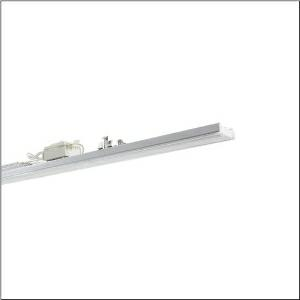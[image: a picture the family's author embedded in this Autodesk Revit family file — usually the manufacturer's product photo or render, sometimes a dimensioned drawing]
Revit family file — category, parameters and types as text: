
# Revit family: licross_11_recessed_ho_51tl18cn4c5m
name_source: partatom
category: Lighting Fixtures
units: mm (PartAtom-declared; Revit-internal decimal feet)

## family parameters
Cut with Voids When Loaded = No
Host = Face
Light Source = No
Part Type = Normal
Room Calculation Point = No
Round Connector Dimension = Use Diameter
Shared = No

## types (1)
- --- (1 x LED, 12610 lm, 66.5 W, 4000K)
    Apparent Load = 67 VA
    CIE Flux Codes = 78 94 99 100 100
    Color Rendering = 80
    Color Temperature = 4000K
    Default Elevation = 1800 mm
    Description = Licross 11 Recessed HO, luminaire insert, of sheet steel, coil coated, white, length: 1.500mm, width: 66mm, height: 67mm, LED rated luminous flux: 12.610lm, light colour: 840, SDCM (Standard Deviation of Colour Matching)MacAdam ≤ 2 SDCM (initial), control gear: ON/OFF Multilumen, CLOi, with plug, 3-pole, with phase selection, mains connection: 220..240V, AC, 50/60Hz, start of lifetime: 67W, end of service life: 75W, internal wiring halogen-free, primary light control with lens, of plastic, primary optical cover: cover, of PMMA, light emission: direct distribution, primary light characteristic: symmetric, protection rating (complete): IP40, insulation class (complete): insulation class I (protective earthing), certification: CE, ENEC, VDE, UKCA, protection symbol: D if used in an environment without relevant dust loads with corresponding accessories, impact resistance: IK06, permissible ambient temperature for indoor applications: -35..+35°C, corresponds to IFS (International Featured Standards) requirements for safety and quality in the food industry, reducing of maximum allowable ambient temperature of 5°C with ceiling mounting, LABS conformity tested according to VDMA 24364:2018-05, The light source and the operating device comply with the requirements of the Ecodesign Regulation (EU) 2019/2020 and are replaceable in accordance with this regulation, packaging unit: 1 piece
    Height = 58 mm
    Lamp = 1 x LED
    Lamp Light Flux = 12610 lm
    Lamp Power = 66.5 W
    Lamp count = 1
    Length = 1500 mm
    Luminous efficacy = 190 lm/W
    Manufacturer = Siteco
    ModVariant = No
    Model = 51TL18CN4C5M
    Mounting Place = Ceiling
    Mounting Type = Pendant
    Number of Poles = 1
    OnlyDefault = Yes
    Power Factor = 1
    Product Name = Licross 11 Recessed HO
    Product group = luminaire insert | ceiling pendant
    ProductGroupID = 901
    Protection Class = Protection class I
    Protection Degree = IP 40
    RLX_Detail_Level = 1
    RLX_Emergency_Light_Flux = 0 lm
    RLX_Emergency_Type = 0
    RLX_Emergency_Type_DB = No
    RlxData = <blob elided: 22593 chars, md5=f7666993>
    Socket = socket
    Standby Power = 0 W
    System Light Flux = 12610 lm
    System Power = 67 W
    Type Comments = factory setting: luminous flux: 100 % | (A | C | E) | 156 mA
    Type Image = l_1296930.jpg
    URL = http://relux.com
    VarID = @adj_090027
    Voltage = 0 V
    Weight = 0.00 kg
    Width = 66 mm

## geometry (parser evidence)
native form markers: Blend x4, Sweep x13
no freeform markers — native parametric forms only
